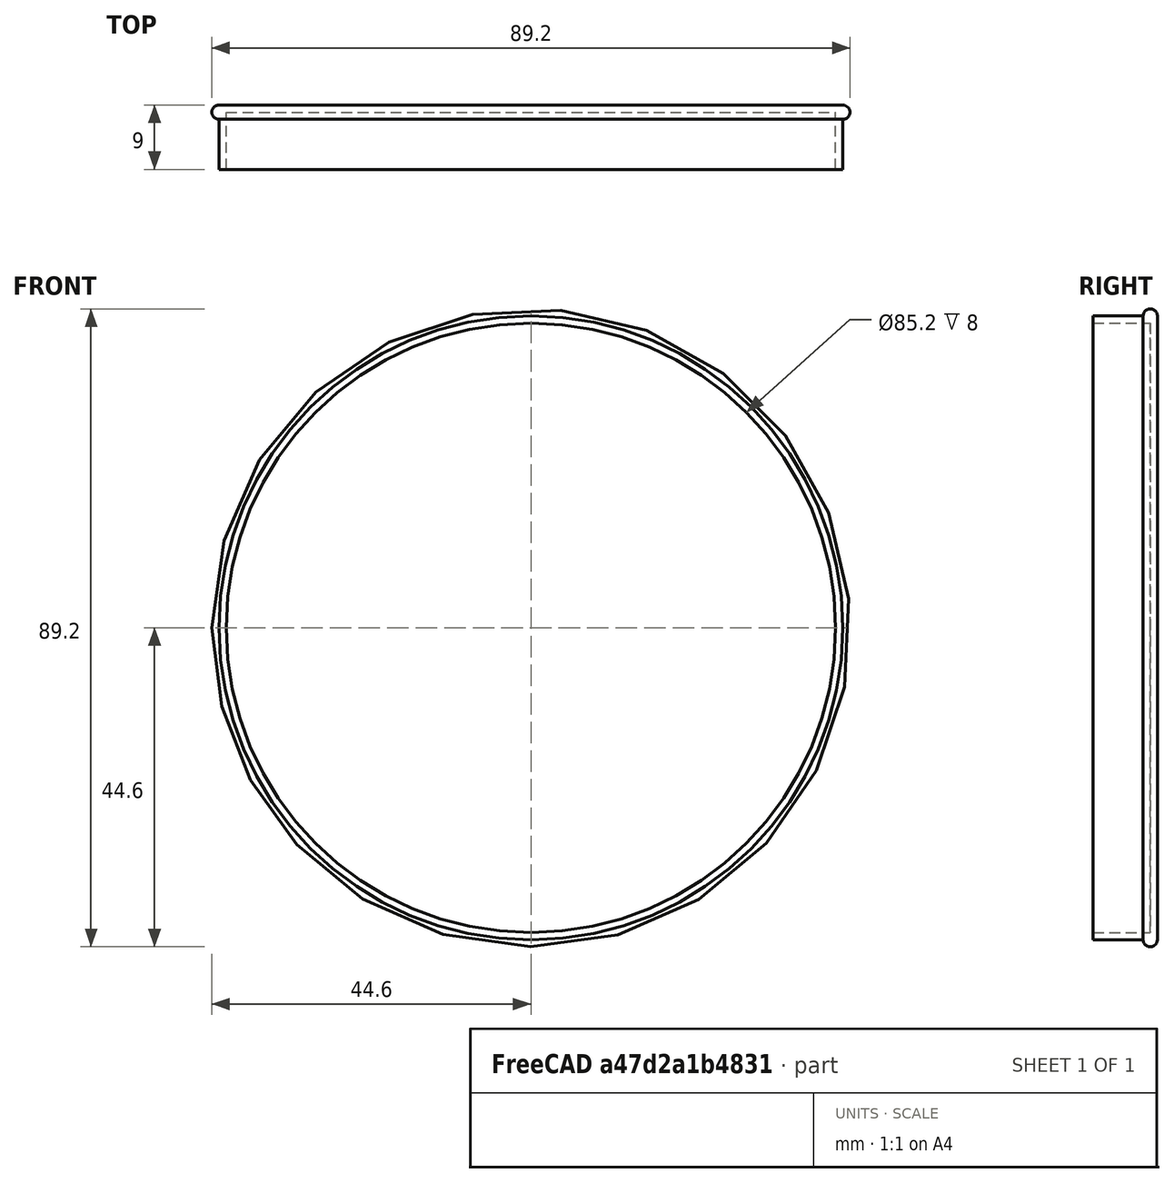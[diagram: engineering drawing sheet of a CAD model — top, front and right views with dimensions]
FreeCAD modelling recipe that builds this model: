
FCSTD DOCUMENT  (FreeCAD 1.1R44874 (Git))
Label: Rollei SL66 - Schneider Xenon 125mm F2 front cap
License: All rights reserved
LicenseURL: https://en.wikipedia.org/wiki/All_rights_reserved
objects: App::Point×1, Sketcher::SketchObject×1, PartDesign::Revolution×1, PartDesign::Body×1
note: 6 computed .brp shape members not serialized (recipe doc carries the construction recipe); baked Part::Feature solids carry a one-line shape summary decoded from their .brp

FEATURE [App::Point] Origin001
  Role = Origin
FEATURE [Sketcher::SketchObject] Sketch
  ArcFitTolerance = 1e-06
  AttachmentSupport = -> [Origin]
  ExternalTypes = [0]
  FullyConstrained = true
  MakeInternals = false
  MapMode = 5
  _ExternalGeoVersion = 1
  sketch-geometry (8):
    g0: LineSegment StartX=-42.6 StartY=0 StartZ=0 EndX=-43.6 EndY=0 EndZ=0
    g1: LineSegment StartX=-43.6 StartY=0 StartZ=0 EndX=-43.6 EndY=7 EndZ=0
    g2: LineSegment StartX=-42.6 StartY=0 StartZ=0 EndX=-42.6 EndY=8 EndZ=0
    g3: LineSegment StartX=-42.6 StartY=8 StartZ=0 EndX=0 EndY=8 EndZ=0
    g4: LineSegment StartX=-43.6 StartY=9 StartZ=0 EndX=0 EndY=9 EndZ=0
    g5: LineSegment StartX=0 StartY=9 StartZ=0 EndX=0 EndY=8 EndZ=0
    g6: LineSegment [constr] StartX=-42.6 StartY=8 StartZ=0 EndX=-42.6 EndY=9 EndZ=0
    g7: ArcOfCircle CenterX=-43.6 CenterY=8 CenterZ=0 NormalX=0 NormalY=0 NormalZ=1 AngleXU=0 Radius=1 StartAngle=1.5708 EndAngle=4.71239
  constraints (25):
    c: Horizontal(g0)
    c: Vertical(g1)
    c: Coincident(g2,g0)
    c: Vertical(g2)
    c: Coincident(g3,g2)
    c: PointOnObject(g3,g-2)
    c: Horizontal(g3)
    c: PointOnObject(g4,g-2)
    c: Horizontal(g4)
    c: Coincident(g5,g3)
    c: Coincident(g5,g4)
    c: Coincident(g0,g1)
    c: Coincident(g6,g2)
    c: PointOnObject(g6,g4)
    c: Equal(g5,g6)
    c: DistanceY(g5,g5) = 1
    c: PointOnObject(g0,g-1)
    c: DistanceY(g2,g2) = 8
    c: Equal(g6,g0)
    c: DistanceX(g3,g3) = 42.6
    c: Coincident(g7,g1)
    c: Coincident(g7,g4)
    c: Vertical(g7,g1)
    c: Vertical(g7,g4)
    c: DistanceY(g1,g2) = 1
FEATURE [PartDesign::Revolution] Revolution
  Angle = 360
  Angle2 = 0
  Axis = (0,1,0)
  Base = (0,0,0)
  FuseOrder = 0
  Profile = -> Sketch
  ReferenceAxis = -> Sketch [V_Axis]
  Refine = true
  Suppressed = false
  Type = 0
FEATURE [PartDesign::Body] Body
  AllowCompound = true
  Group = -> [Sketch,Revolution]
  Origin = -> Origin
  Tip = -> Revolution
